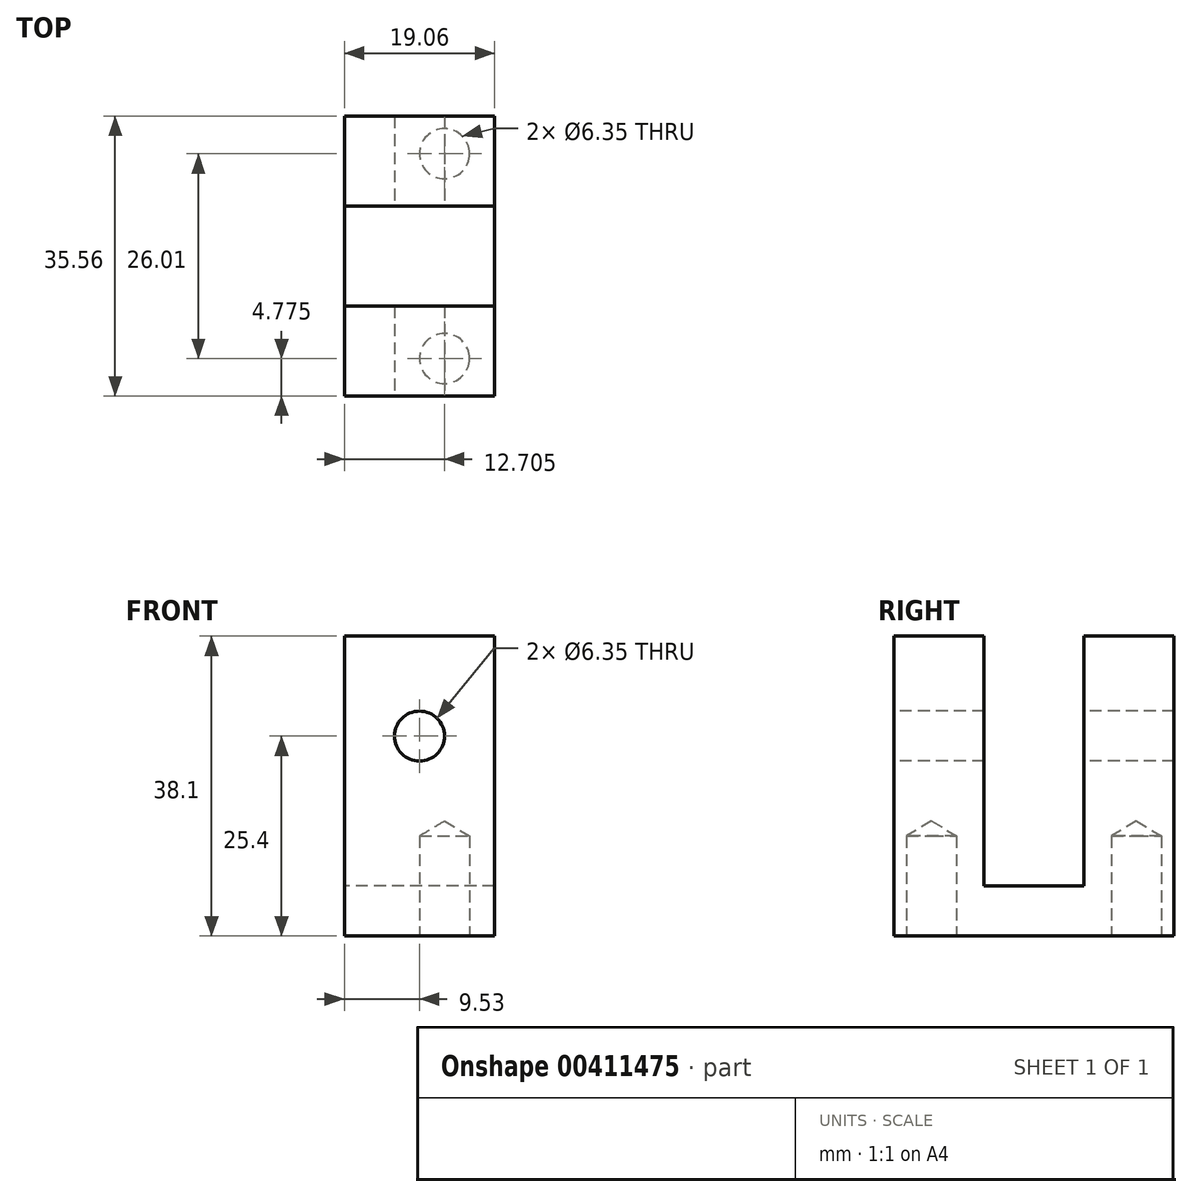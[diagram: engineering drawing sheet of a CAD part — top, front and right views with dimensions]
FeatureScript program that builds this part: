
annotation { "Feature Type Name" : "Feature", "Feature Type Description" : "" }
export const myFeature = defineFeature(function(context is Context, id is Id, definition is map)
    precondition{}
    {
        {
            var Q0;
            Q0=qCreatedBy(makeId("Right.planeOp"),FACE);
            var sketch = newSketch(context, id + "F0", { "sketchPlane" : qUnion([Q0])});
            skLineSegment(sketch, "E0", {"start": v(-17.78, 12.7) * mm, "end": v(-6.35, 12.7) * mm});
            skLineSegment(sketch, "E1", {"start": v(-6.35, 12.7) * mm, "end": v(-6.35, -19.05) * mm});
            skLineSegment(sketch, "E2", {"start": v(-6.35, -19.05) * mm, "end": v(0, -19.05) * mm});
            skLineSegment(sketch, "E3", {"start": v(-17.78, 12.7) * mm, "end": v(-17.78, -25.4) * mm});
            skLineSegment(sketch, "E4", {"start": v(-17.78, -25.4) * mm, "end": v(0, -25.4) * mm});
            skLineSegment(sketch, "E5", {"start": v(0, -25.4) * mm, "end": v(0, -19.05) * mm, "construction": true});
            skLineSegment(sketch, "E6.MirrorCS", {"start": v(6.35, 12.7) * mm, "end": v(6.35, -19.05) * mm});
            skLineSegment(sketch, "E7.MirrorCS", {"start": v(6.35, -19.05) * mm, "end": v(0, -19.05) * mm});
            skLineSegment(sketch, "E8.MirrorCS", {"start": v(17.78, 12.7) * mm, "end": v(6.35, 12.7) * mm});
            skLineSegment(sketch, "E9.MirrorCS", {"start": v(17.78, -25.4) * mm, "end": v(0, -25.4) * mm});
            skLineSegment(sketch, "E10.MirrorCS", {"start": v(17.78, 12.7) * mm, "end": v(17.78, -25.4) * mm});
            skSolve(sketch);
        }
        {
            var Q0;
            Q0=makeQuery(id+"F0.imprint","IMPRINT",FACE,{"disambiguationData":[TD([[makeQuery(id+"F0.imprint","IMPRINT",EDGE,{"derivedFrom":sQuery(id+"F0.wireOp",EDGE,"E0")}),-1.0]])]});
            extrude(context, id + "F1", {"entities" : qUnion([Q0]), "endBound" : BoundingType.SYMMETRIC, "depth" : 19.05 * mm});
        }
        {
            var Q0;
            Q0=makeQuery(id+"F1.opExtrude","SWEPT_FACE",FACE,{"disambiguationData":[OSD([sQuery(id+"F0.wireOp",EDGE,"E4"),sQuery(id+"F0.wireOp",EDGE,"E9.MirrorCS")])]});
            var sketch = newSketch(context, id + "F2", { "sketchPlane" : qUnion([Q0])});
            skLineSegment(sketch, "E11", {"start": v(9.53, 0) * mm, "end": v(-9.53, 0) * mm, "construction": true});
            skPoint(sketch, "E12", {"position": v(3.17, 13) * mm});
            skPoint(sketch, "E13.MirrorP", {"position": v(3.17, -13) * mm});
            skSolve(sketch);
        }
        {
            var Q0;
            Q0=sQuery(id+"F2.wireOp",VERTEX,"E12");
            var Q1;
            Q1=sQuery(id+"F2.wireOp",VERTEX,"E13.MirrorP");
            var Q2;
            Q2=makeQuery(id+"F1.opExtrude","SWEPT_BODY",BODY,{"disambiguationData":[OSD([sQuery(id+"F0.wireOp",EDGE,"E0"),sQuery(id+"F0.wireOp",EDGE,"E1"),sQuery(id+"F0.wireOp",EDGE,"E2"),sQuery(id+"F0.wireOp",EDGE,"E3"),sQuery(id+"F0.wireOp",EDGE,"E4"),sQuery(id+"F0.wireOp",EDGE,"E6.MirrorCS"),sQuery(id+"F0.wireOp",EDGE,"E7.MirrorCS"),sQuery(id+"F0.wireOp",EDGE,"E8.MirrorCS"),sQuery(id+"F0.wireOp",EDGE,"E9.MirrorCS"),sQuery(id+"F0.wireOp",EDGE,"E10.MirrorCS")])]});
            hole(context, id + "F3", {"style" : HoleStyle.SIMPLE, "endStyle" : HoleEndStyle.BLIND, "holeDiameter" : 6.35 * mm, "holeDepth" : 12.7 * mm, "isTappedThrough" : true, "tappedDepth" : 12.7 * mm, "tapClearance" : 3, "locations" : qUnion([Q0, Q1]), "scope" : qUnion([Q2])});
        }
        {
            var Q0;
            Q0=makeQuery(id+"F1.opExtrude","SWEPT_FACE",FACE,{"disambiguationData":[OSD([sQuery(id+"F0.wireOp",EDGE,"E3")])]});
            var sketch = newSketch(context, id + "F4", { "sketchPlane" : qUnion([Q0])});
            skCircle(sketch, "E14", {"center": v(0, 0) * mm, "radius": 3.18 * mm});
            skSolve(sketch);
        }
        {
            var Q0;
            Q0 = qSketchRegion(id + "F4", true);
            extrude(context, id + "F5", {"entities" : qUnion([Q0]), "operationType" : NewBodyOperationType.REMOVE, "endBound" : BoundingType.THROUGH_ALL, "oppositeDirection" : true, "depth" : 25.4 * mm});
        }
    });
